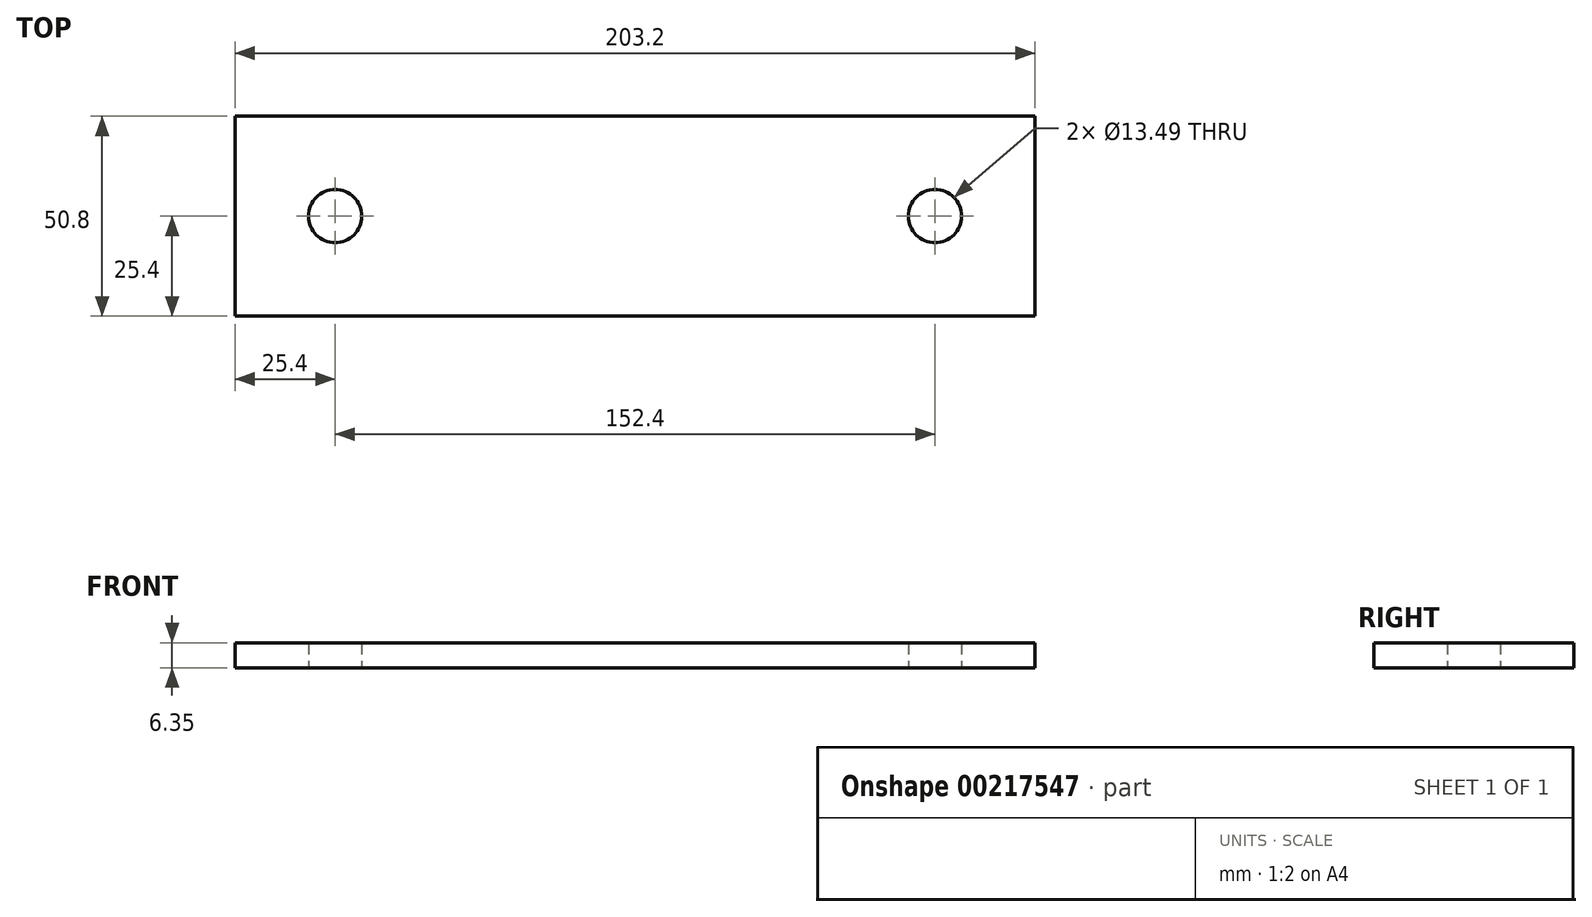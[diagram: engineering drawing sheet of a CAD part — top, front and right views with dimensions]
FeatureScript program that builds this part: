
annotation { "Feature Type Name" : "Feature", "Feature Type Description" : "" }
export const myFeature = defineFeature(function(context is Context, id is Id, definition is map)
    precondition{}
    {
        {
            var Q0;
            Q0=qCreatedBy(makeId("Top.planeOp"),FACE);
            var sketch = newSketch(context, id + "F0", { "sketchPlane" : qUnion([Q0])});
            skLineSegment(sketch, "E0.bottom", {"start": v(0, 0) * mm, "end": v(203.2, 0) * mm});
            skLineSegment(sketch, "E0.top", {"start": v(0, 50.8) * mm, "end": v(203.2, 50.8) * mm});
            skLineSegment(sketch, "E0.left", {"start": v(0, 0) * mm, "end": v(0, 50.8) * mm});
            skLineSegment(sketch, "E0.right", {"start": v(203.2, 0) * mm, "end": v(203.2, 50.8) * mm});
            skCircle(sketch, "E1", {"center": v(25.4, 25.4) * mm, "radius": 6.75 * mm});
            skCircle(sketch, "E2", {"center": v(177.8, 25.4) * mm, "radius": 6.75 * mm});
            skSolve(sketch);
        }
        {
            var Q0;
            Q0=makeQuery(id+"F0.imprint","IMPRINT",FACE,{"disambiguationData":[TD([[makeQuery(id+"F0.imprint","IMPRINT",EDGE,{"derivedFrom":sQuery(id+"F0.wireOp",EDGE,"E0.bottom")}),1.0]])]});
            extrude(context, id + "F1", {"entities" : qUnion([Q0]), "depth" : 6.35 * mm});
        }
    });
